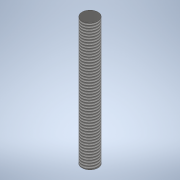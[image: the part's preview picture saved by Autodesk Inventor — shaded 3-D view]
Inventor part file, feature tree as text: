
AUTODESK INVENTOR PART (.ipt)
format: ipt  version: 2021 (Build 250183000, 183)  size: 101,888 bytes
history: native  units: mm
features: extrude x1, thread x1, sketch x1
ambient origin geometry x8: Origin, YZ Plane, XZ Plane, XY Plane, X Axis, Y Axis, Z Axis, Center Point
bodies: Solid1 (feature_tree)
feature tree (3):
  extrude  "Extrusion1"  Depth=64.0mm TaperAngle=0.0deg
  thread  "Thread2"  [1 undecoded]
  sketch  "Sketch1"  dims[d0=8.0mm d1=64.0mm d2=0.0mm d9=64.0mm d10=0.0mm]
note: 1 required parameter value undecoded (feature->parameter linkage not recoverable at this tier; creation-order binding heuristic only, values carry confidence <= 0.55)
